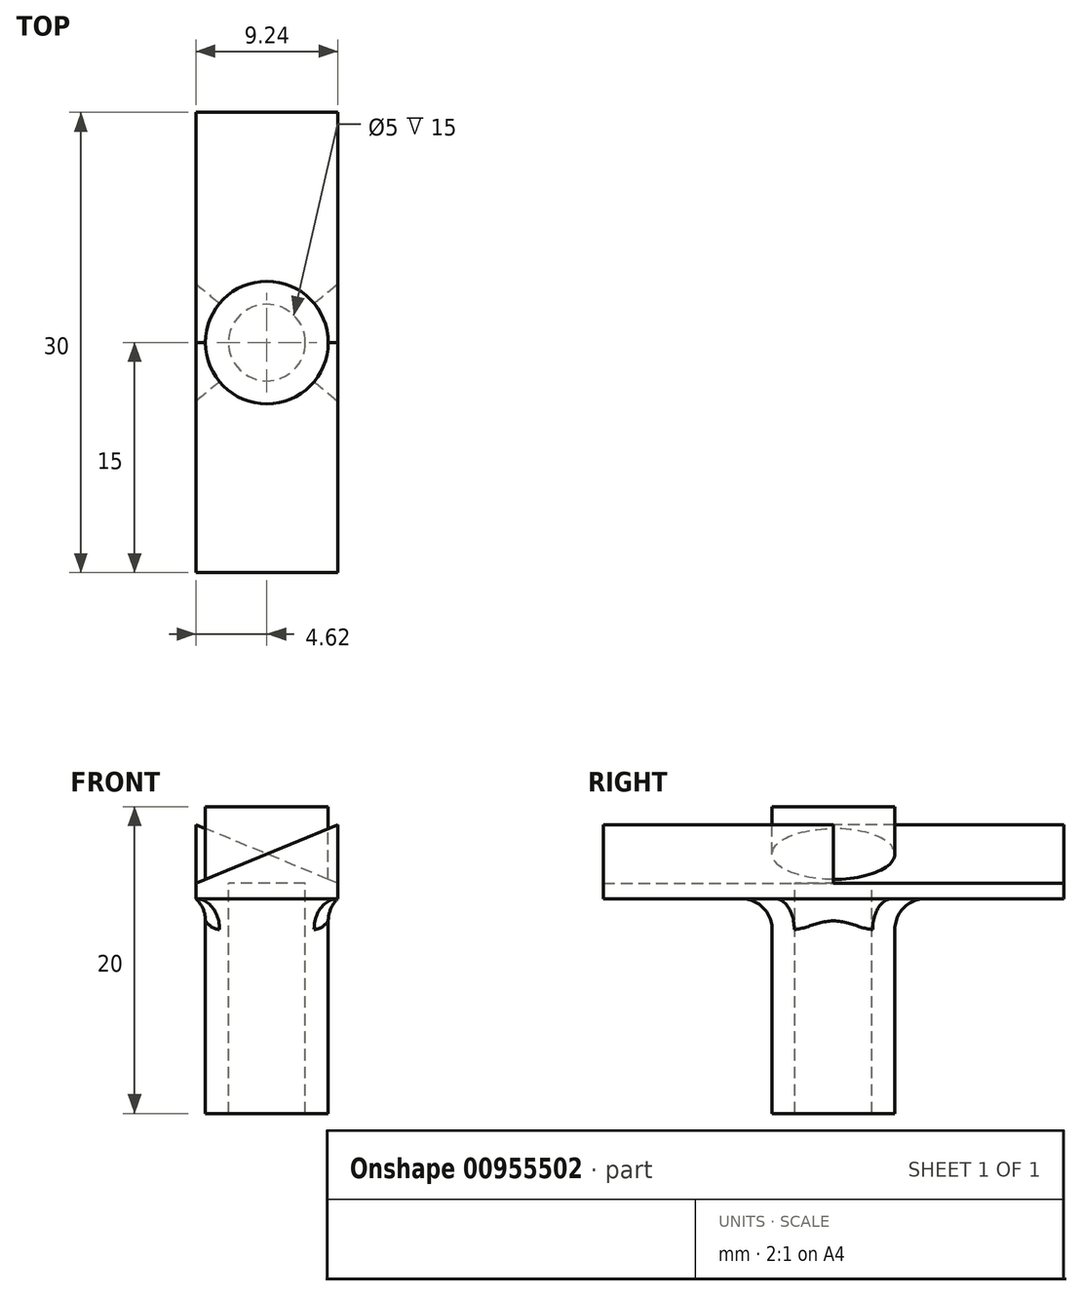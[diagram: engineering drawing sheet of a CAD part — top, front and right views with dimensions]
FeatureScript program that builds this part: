
annotation { "Feature Type Name" : "Feature", "Feature Type Description" : "" }
export const myFeature = defineFeature(function(context is Context, id is Id, definition is map)
    precondition{}
    {
        {
            var Q0;
            Q0=qCreatedBy(makeId("Front.planeOp"),FACE);
            var sketch = newSketch(context, id + "F0", { "sketchPlane" : qUnion([Q0])});
            skLineSegment(sketch, "E0", {"start": v(-4.62, 0) * mm, "end": v(4.62, 3.83) * mm});
            skLineSegment(sketch, "E1", {"start": v(4.62, 3.83) * mm, "end": v(4.62, -1) * mm});
            skLineSegment(sketch, "E2", {"start": v(4.62, -1) * mm, "end": v(-4.62, -1) * mm});
            skLineSegment(sketch, "E3", {"start": v(-4.62, -1) * mm, "end": v(-4.62, 0) * mm});
            skPoint(sketch, "E4", {"position": v(0, 1.91) * mm});
            skSolve(sketch);
        }
        {
            var Q0;
            Q0=makeQuery(id+"F0.imprint","IMPRINT",FACE,{"disambiguationData":[TD([[makeQuery(id+"F0.imprint","IMPRINT",EDGE,{"derivedFrom":sQuery(id+"F0.wireOp",EDGE,"E0")}),-1.0]])]});
            extrude(context, id + "F1", {"entities" : qUnion([Q0]), "depth" : 15 * mm, "offsetDistance" : 25 * mm});
        }
        {
            var Q0;
            Q0=qCreatedBy(makeId("Front.planeOp"),FACE);
            var sketch = newSketch(context, id + "F2", { "sketchPlane" : qUnion([Q0])});
            skLineSegment(sketch, "E5", {"start": v(0, 0) * mm, "end": v(0, 45.35) * mm, "construction": true});
            skSolve(sketch);
        }
        {
            var Q0;
            Q0=makeQuery(id+"F1.opExtrude","SWEPT_BODY",BODY,{"disambiguationData":[OSD([sQuery(id+"F0.wireOp",EDGE,"E0"),sQuery(id+"F0.wireOp",EDGE,"E1"),sQuery(id+"F0.wireOp",EDGE,"E2"),sQuery(id+"F0.wireOp",EDGE,"E3")])]});
            var Q1;
            Q1=sQuery(id+"F2.wireOp",EDGE,"E5");
            circularPattern(context, id + "F3", {"entities" : qUnion([Q0]), "axis" : qUnion([Q1]), "angle" : 360 * degree, "instanceCount" : 2, "equalSpace" : true});
        }
        {
            var Q0;
            Q0=qCreatedBy(makeId("Top.planeOp"),FACE);
            var sketch = newSketch(context, id + "F4", { "sketchPlane" : qUnion([Q0])});
            skCircle(sketch, "E6", {"center": v(0, 0) * mm, "radius": 4 * mm});
            skSolve(sketch);
        }
        {
            var Q0;
            Q0 = qSketchRegion(id + "F4", true);
            extrude(context, id + "F5", {"entities" : qUnion([Q0]), "oppositeDirection" : true, "depth" : 15 * mm, "offsetDistance" : 25 * mm, "hasSecondDirection" : true, "secondDirectionOppositeDirection" : false, "secondDirectionDepth" : 5 * mm});
        }
        {
            var Q0;
            Q0=makeQuery(id+"F5.opExtrude","SWEPT_BODY",BODY,{"disambiguationData":[OSD([sQuery(id+"F4.wireOp",EDGE,"E6")])]});
            var Q1;
            Q1=makeQuery(id+"F3.opPattern","COPY",BODY,{"derivedFrom":makeQuery(id+"F1.opExtrude","SWEPT_BODY",BODY,{"disambiguationData":[OSD([sQuery(id+"F0.wireOp",EDGE,"E0"),sQuery(id+"F0.wireOp",EDGE,"E1"),sQuery(id+"F0.wireOp",EDGE,"E2"),sQuery(id+"F0.wireOp",EDGE,"E3")])]}),"instanceName":"1"});
            var Q2;
            Q2=makeQuery(id+"F1.opExtrude","SWEPT_BODY",BODY,{"disambiguationData":[OSD([sQuery(id+"F0.wireOp",EDGE,"E0"),sQuery(id+"F0.wireOp",EDGE,"E1"),sQuery(id+"F0.wireOp",EDGE,"E2"),sQuery(id+"F0.wireOp",EDGE,"E3")])]});
            booleanBodies(context, id + "F6", {"operationType" : BooleanOperationType.UNION, "tools" : qUnion([Q0, Q1, Q2])});
        }
        {
            var Q0;
            Q0=qCreatedBy(makeId("Top.planeOp"),FACE);
            var sketch = newSketch(context, id + "F7", { "sketchPlane" : qUnion([Q0])});
            skCircle(sketch, "E7", {"center": v(0, 0) * mm, "radius": 2.5 * mm});
            skSolve(sketch);
        }
        {
            var Q0;
            Q0 = qSketchRegion(id + "F7", true);
            extrude(context, id + "F8", {"entities" : qUnion([Q0]), "operationType" : NewBodyOperationType.REMOVE, "oppositeDirection" : true, "depth" : 25 * mm, "offsetDistance" : 25 * mm});
        }
        {
            var Q0;
            Q0=makeQuery(id+"F6.opBoolean","INTERSECT",EDGE,{"derivedFrom":[makeQuery(id+"F1.opExtrude","SWEPT_FACE",FACE,{"disambiguationData":[OSD([sQuery(id+"F0.wireOp",EDGE,"E2")])]}),makeQuery(id+"F5.opExtrude","SWEPT_FACE",FACE,{"disambiguationData":[OSD([sQuery(id+"F4.wireOp",EDGE,"E6")])]})]});
            fillet(context, id + "F9", {"entities" : qUnion([Q0]), "radius" : 2 * mm, "tangentPropagation" : true, "allowEdgeOverflow" : false});
        }
    });
